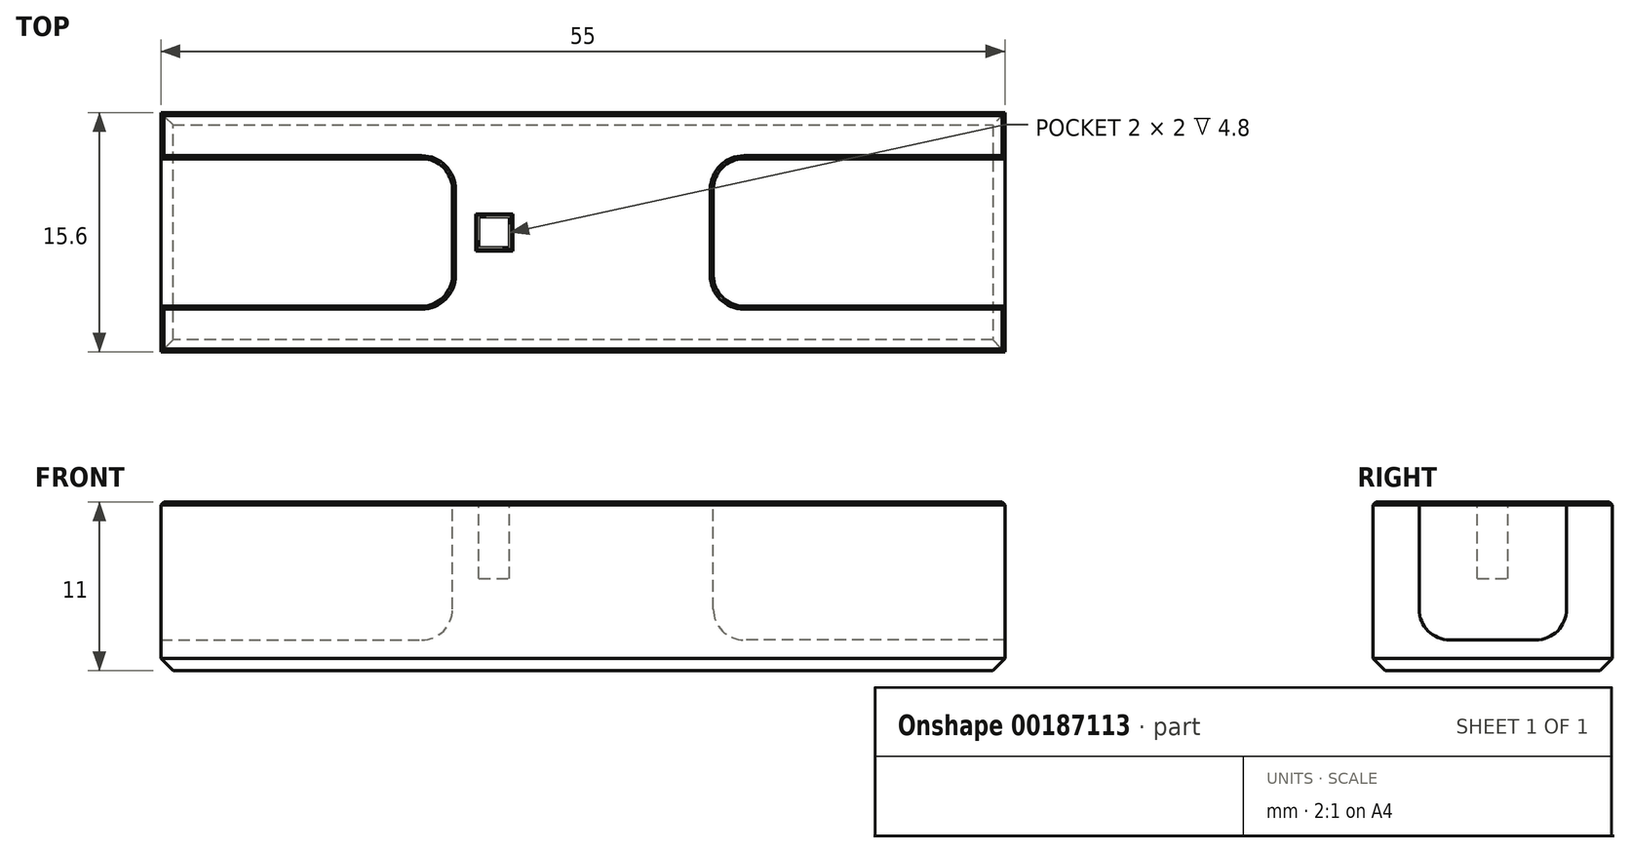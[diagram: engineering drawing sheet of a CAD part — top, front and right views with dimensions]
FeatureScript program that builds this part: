
annotation { "Feature Type Name" : "Feature", "Feature Type Description" : "" }
export const myFeature = defineFeature(function(context is Context, id is Id, definition is map)
    precondition{}
    {
        {
            var Q0;
            Q0=qCreatedBy(makeId("Top.planeOp"),FACE);
            var sketch = newSketch(context, id + "F0", { "sketchPlane" : qUnion([Q0])});
            skLineSegment(sketch, "E0.rect.bottom", {"start": v(27.5, 7.8) * mm, "end": v(-27.5, 7.8) * mm});
            skLineSegment(sketch, "E0.rect.top", {"start": v(27.5, -7.8) * mm, "end": v(-27.5, -7.8) * mm});
            skLineSegment(sketch, "E0.rect.left", {"start": v(27.5, 7.8) * mm, "end": v(27.5, -7.8) * mm});
            skLineSegment(sketch, "E0.rect.right", {"start": v(-27.5, 7.8) * mm, "end": v(-27.5, -7.8) * mm});
            skPoint(sketch, "E0.rect.middle", {"position": v(0, 0) * mm});
            skSolve(sketch);
        }
        {
            var Q0;
            Q0=qSketchRegion(id+"F0",true);
            extrude(context, id + "F1", {"entities" : qUnion([Q0]), "depth" : 11 * mm});
        }
        {
            var Q0;
            Q0=makeQuery(id+"F1.opExtrude","CAP_FACE",FACE,{"disambiguationData":[OSD([sQuery(id+"F0.wireOp",EDGE,"E0.rect.bottom"),sQuery(id+"F0.wireOp",EDGE,"E0.rect.top"),sQuery(id+"F0.wireOp",EDGE,"E0.rect.left"),sQuery(id+"F0.wireOp",EDGE,"E0.rect.right")])],"isStart":false});
            var sketch = newSketch(context, id + "F2", { "sketchPlane" : qUnion([Q0])});
            skLineSegment(sketch, "E1.bottom", {"start": v(-6.77, -1) * mm, "end": v(-4.77, -1) * mm});
            skLineSegment(sketch, "E1.top", {"start": v(-6.77, 1) * mm, "end": v(-4.77, 1) * mm});
            skLineSegment(sketch, "E1.left", {"start": v(-6.77, -1) * mm, "end": v(-6.77, 1) * mm});
            skLineSegment(sketch, "E1.right", {"start": v(-4.77, -1) * mm, "end": v(-4.77, 1) * mm});
            skPoint(sketch, "E1.middle", {"position": v(-5.77, 0) * mm});
            skSolve(sketch);
        }
        {
            var Q0;
            Q0=makeQuery(id+"F2.imprint","IMPRINT",FACE,{"disambiguationData":[TD([[makeQuery(id+"F2.imprint","IMPRINT",EDGE,{"derivedFrom":sQuery(id+"F2.wireOp",EDGE,"E1.bottom")}),1.0]])]});
            var Q1;
            Q1=makeQuery(id+"F1.opExtrude","CAP_FACE",FACE,{"disambiguationData":[OSD([sQuery(id+"F0.wireOp",EDGE,"E0.rect.bottom"),sQuery(id+"F0.wireOp",EDGE,"E0.rect.top"),sQuery(id+"F0.wireOp",EDGE,"E0.rect.left"),sQuery(id+"F0.wireOp",EDGE,"E0.rect.right")])],"isStart":false});
            extrude(context, id + "F3", {"entities" : qUnion([Q0]), "operationType" : NewBodyOperationType.REMOVE, "oppositeDirection" : true, "endBoundEntityFace" : qUnion([Q1]), "depth" : 5 * mm});
        }
        {
            var Q0;
            Q0=makeQuery(id+"F1.opExtrude","CAP_FACE",FACE,{"disambiguationData":[OSD([sQuery(id+"F0.wireOp",EDGE,"E0.rect.bottom"),sQuery(id+"F0.wireOp",EDGE,"E0.rect.top"),sQuery(id+"F0.wireOp",EDGE,"E0.rect.left"),sQuery(id+"F0.wireOp",EDGE,"E0.rect.right")])],"isStart":false});
            var sketch = newSketch(context, id + "F4", { "sketchPlane" : qUnion([Q0])});
            skLineSegment(sketch, "E2", {"start": v(-27.5, 0) * mm, "end": v(27.5, 0) * mm, "construction": true});
            skLineSegment(sketch, "E3", {"start": v(0, 7.8) * mm, "end": v(0, -7.8) * mm, "construction": true});
            skLineSegment(sketch, "E4.rect.bottom", {"start": v(-27.5, 4.8) * mm, "end": v(-8.5, 4.8) * mm});
            skLineSegment(sketch, "E4.rect.top", {"start": v(-27.5, -4.8) * mm, "end": v(-8.5, -4.8) * mm});
            skLineSegment(sketch, "E4.rect.left", {"start": v(-27.5, 4.8) * mm, "end": v(-27.5, -4.8) * mm});
            skLineSegment(sketch, "E4.rect.right", {"start": v(-8.5, 4.8) * mm, "end": v(-8.5, -4.8) * mm});
            skPoint(sketch, "E4.rect.middle", {"position": v(-18, 0) * mm});
            skLineSegment(sketch, "E5.MirrorCS", {"start": v(27.5, 4.8) * mm, "end": v(8.5, 4.8) * mm});
            skLineSegment(sketch, "E6.MirrorCS", {"start": v(27.5, -4.8) * mm, "end": v(8.5, -4.8) * mm});
            skLineSegment(sketch, "E7.MirrorCS", {"start": v(8.5, 4.8) * mm, "end": v(8.5, -4.8) * mm});
            skLineSegment(sketch, "E8.MirrorCS", {"start": v(27.5, 4.8) * mm, "end": v(27.5, -4.8) * mm});
            skPoint(sketch, "E9.MirrorP", {"position": v(18, 0) * mm});
            skSolve(sketch);
        }
        {
            var Q0;
            Q0=qSketchRegion(id+"F4",true);
            extrude(context, id + "F5", {"entities" : qUnion([Q0]), "operationType" : NewBodyOperationType.REMOVE, "oppositeDirection" : true, "depth" : 9 * mm});
        }
        {
            var Q0;
            Q0=makeQuery(id+"F5.boolean.opBoolean","COPY",EDGE,{"derivedFrom":makeQuery(id+"F5.opExtrude","SWEPT_EDGE",EDGE,{"disambiguationData":[OSD([sQuery(id+"F4.wireOp",EDGE,"E4.rect.bottom"),sQuery(id+"F4.wireOp",EDGE,"E4.rect.right")])]})});
            var Q1;
            Q1=makeQuery(id+"F5.boolean.opBoolean","COPY",EDGE,{"derivedFrom":makeQuery(id+"F5.opExtrude","CAP_EDGE",EDGE,{"disambiguationData":[OSD([sQuery(id+"F4.wireOp",EDGE,"E4.rect.bottom")])],"isStart":false})});
            var Q2;
            Q2=makeQuery(id+"F5.boolean.opBoolean","COPY",EDGE,{"derivedFrom":makeQuery(id+"F5.opExtrude","CAP_EDGE",EDGE,{"disambiguationData":[OSD([sQuery(id+"F4.wireOp",EDGE,"E4.rect.right")])],"isStart":false})});
            var Q3;
            Q3=makeQuery(id+"F5.boolean.opBoolean","COPY",EDGE,{"derivedFrom":makeQuery(id+"F5.opExtrude","CAP_EDGE",EDGE,{"disambiguationData":[OSD([sQuery(id+"F4.wireOp",EDGE,"E4.rect.top")])],"isStart":false})});
            var Q4;
            Q4=makeQuery(id+"F5.boolean.opBoolean","COPY",EDGE,{"derivedFrom":makeQuery(id+"F5.opExtrude","SWEPT_EDGE",EDGE,{"disambiguationData":[OSD([sQuery(id+"F4.wireOp",EDGE,"E4.rect.top"),sQuery(id+"F4.wireOp",EDGE,"E4.rect.right")])]})});
            var Q5;
            Q5=makeQuery(id+"F5.boolean.opBoolean","COPY",EDGE,{"derivedFrom":makeQuery(id+"F5.opExtrude","CAP_EDGE",EDGE,{"disambiguationData":[OSD([sQuery(id+"F4.wireOp",EDGE,"E7.MirrorCS")])],"isStart":false})});
            var Q6;
            Q6=makeQuery(id+"F5.boolean.opBoolean","COPY",EDGE,{"derivedFrom":makeQuery(id+"F5.opExtrude","SWEPT_EDGE",EDGE,{"disambiguationData":[OSD([sQuery(id+"F4.wireOp",EDGE,"E5.MirrorCS"),sQuery(id+"F4.wireOp",EDGE,"E7.MirrorCS")])]})});
            var Q7;
            Q7=makeQuery(id+"F5.boolean.opBoolean","COPY",EDGE,{"derivedFrom":makeQuery(id+"F5.opExtrude","CAP_EDGE",EDGE,{"disambiguationData":[OSD([sQuery(id+"F4.wireOp",EDGE,"E5.MirrorCS")])],"isStart":false})});
            var Q8;
            Q8=makeQuery(id+"F5.boolean.opBoolean","COPY",EDGE,{"derivedFrom":makeQuery(id+"F5.opExtrude","CAP_EDGE",EDGE,{"disambiguationData":[OSD([sQuery(id+"F4.wireOp",EDGE,"E6.MirrorCS")])],"isStart":false})});
            var Q9;
            Q9=makeQuery(id+"F5.boolean.opBoolean","COPY",EDGE,{"derivedFrom":makeQuery(id+"F5.opExtrude","SWEPT_EDGE",EDGE,{"disambiguationData":[OSD([sQuery(id+"F4.wireOp",EDGE,"E6.MirrorCS"),sQuery(id+"F4.wireOp",EDGE,"E7.MirrorCS")])]})});
            fillet(context, id + "F6", {"entities" : qUnion([Q0, Q1, Q2, Q3, Q4, Q5, Q6, Q7, Q8, Q9]), "radius" : 2 * mm, "tangentPropagation" : true, "allowEdgeOverflow" : false});
        }
        {
            var Q0;
            Q0=makeQuery(id+"F1.opExtrude","CAP_FACE",FACE,{"disambiguationData":[OSD([sQuery(id+"F0.wireOp",EDGE,"E0.rect.bottom"),sQuery(id+"F0.wireOp",EDGE,"E0.rect.top"),sQuery(id+"F0.wireOp",EDGE,"E0.rect.left"),sQuery(id+"F0.wireOp",EDGE,"E0.rect.right")])],"isStart":false});
            chamfer(context, id + "F7", {"entities" : qUnion([Q0]), "width" : 0.2 * mm, "tangentPropagation" : true});
        }
        {
            var Q0;
            Q0=makeQuery(id+"F1.opExtrude","CAP_FACE",FACE,{"disambiguationData":[OSD([sQuery(id+"F0.wireOp",EDGE,"E0.rect.bottom"),sQuery(id+"F0.wireOp",EDGE,"E0.rect.top"),sQuery(id+"F0.wireOp",EDGE,"E0.rect.left"),sQuery(id+"F0.wireOp",EDGE,"E0.rect.right")])],"isStart":true});
            chamfer(context, id + "F8", {"entities" : qUnion([Q0]), "width" : 0.8 * mm, "tangentPropagation" : true});
        }
    });
